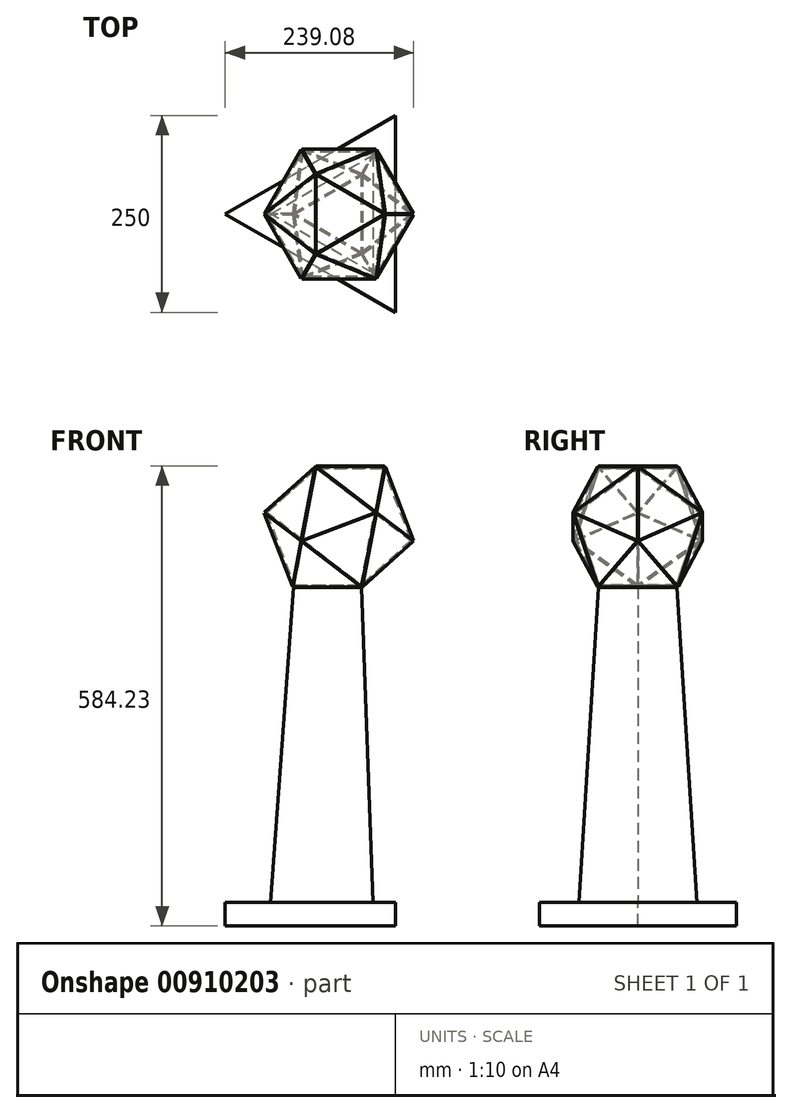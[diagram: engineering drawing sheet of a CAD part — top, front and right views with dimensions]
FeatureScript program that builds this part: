
annotation { "Feature Type Name" : "Feature", "Feature Type Description" : "" }
export const myFeature = defineFeature(function(context is Context, id is Id, definition is map)
    precondition{}
    {
        {
            var Q0;
            Q0=qCreatedBy(makeId("Top.planeOp"),FACE);
            var sketch = newSketch(context, id + "F0", { "sketchPlane" : qUnion([Q0])});
            skCircle(sketch, "E0.cCircle", {"center": v(0, 0) * mm, "radius": 28.87 * mm, "construction": true});
            skLineSegment(sketch, "E0.0", {"start": v(28.87, 50) * mm, "end": v(28.87, -50) * mm});
            skLineSegment(sketch, "E0.1", {"start": v(28.87, -50) * mm, "end": v(-57.74, 0) * mm});
            skLineSegment(sketch, "E0.2", {"start": v(-57.74, 0) * mm, "end": v(28.87, 50) * mm});
            skPoint(sketch, "E0.0.midPoint", {"position": v(28.87, 0) * mm});
            skSolve(sketch);
        }
        {
            var Q0;
            Q0=makeQuery(id+"F0.imprint","IMPRINT",FACE,{"disambiguationData":[TD([[makeQuery(id+"F0.imprint","IMPRINT",EDGE,{"derivedFrom":sQuery(id+"F0.wireOp",EDGE,"E0.0")}),-1.0]])]});
            extrude(context, id + "F1", {"entities" : qUnion([Q0]), "depth" : 3 * mm, "offsetDistance" : 25 * mm});
        }
        {
            var Q0;
            Q0=makeQuery(id+"F1.opExtrude","SWEPT_BODY",BODY,{"disambiguationData":[OSD([sQuery(id+"F0.wireOp",EDGE,"E0.0"),sQuery(id+"F0.wireOp",EDGE,"E0.1"),sQuery(id+"F0.wireOp",EDGE,"E0.2")])]});
            transform(context, id + "F2", {"entities" : qUnion([Q0]), "transformType" : TransformType.TRANSLATION_3D, "dx" : 0 * mm, "dy" : 0 * mm, "dz" : 0 * mm, "makeCopy" : true});
        }
        {
            var Q0;
            Q0=makeQuery(id+"F1.opExtrude","SWEPT_FACE",FACE,{"disambiguationData":[OSD([sQuery(id+"F0.wireOp",EDGE,"E0.1")])]});
            var sketch = newSketch(context, id + "F3", { "sketchPlane" : qUnion([Q0])});
            skLineSegment(sketch, "E1", {"start": v(-50, 1.5) * mm, "end": v(50, 1.5) * mm});
            skSolve(sketch);
        }
        {
            var Q0;
            Q0=makeQuery(id+"F2.opPattern","COPY",BODY,{"derivedFrom":makeQuery(id+"F1.opExtrude","SWEPT_BODY",BODY,{"disambiguationData":[OSD([sQuery(id+"F0.wireOp",EDGE,"E0.0"),sQuery(id+"F0.wireOp",EDGE,"E0.1"),sQuery(id+"F0.wireOp",EDGE,"E0.2")])]}),"instanceName":"1"});
            var Q1;
            Q1=sQuery(id+"F3.wireOp",EDGE,"E1");
            transform(context, id + "F4", {"entities" : qUnion([Q0]), "transformType" : TransformType.ROTATION, "transformAxis" : qUnion([Q1]), "angle" : 138.2 * degree, "makeCopy" : false});
        }
        {
            var Q0;
            Q0=makeQuery(id+"F1.opExtrude","SWEPT_BODY",BODY,{"disambiguationData":[OSD([sQuery(id+"F0.wireOp",EDGE,"E0.0"),sQuery(id+"F0.wireOp",EDGE,"E0.1"),sQuery(id+"F0.wireOp",EDGE,"E0.2")])]});
            transform(context, id + "F5", {"entities" : qUnion([Q0]), "transformType" : TransformType.TRANSLATION_3D, "dx" : 0 * mm, "dy" : 0 * mm, "dz" : 0 * mm, "makeCopy" : true});
        }
        {
            var Q0;
            Q0=makeQuery(id+"F1.opExtrude","SWEPT_FACE",FACE,{"disambiguationData":[OSD([sQuery(id+"F0.wireOp",EDGE,"E0.0")])]});
            var sketch = newSketch(context, id + "F6", { "sketchPlane" : qUnion([Q0])});
            skLineSegment(sketch, "E2", {"start": v(-50, 1.5) * mm, "end": v(50, 1.5) * mm});
            skSolve(sketch);
        }
        {
            var Q0;
            Q0=makeQuery(id+"F5.opPattern","COPY",BODY,{"derivedFrom":makeQuery(id+"F1.opExtrude","SWEPT_BODY",BODY,{"disambiguationData":[OSD([sQuery(id+"F0.wireOp",EDGE,"E0.0"),sQuery(id+"F0.wireOp",EDGE,"E0.1"),sQuery(id+"F0.wireOp",EDGE,"E0.2")])]}),"instanceName":"1"});
            var Q1;
            Q1=sQuery(id+"F6.wireOp",EDGE,"E2");
            transform(context, id + "F7", {"entities" : qUnion([Q0]), "transformType" : TransformType.ROTATION, "transformAxis" : qUnion([Q1]), "angle" : 138.2 * degree, "makeCopy" : false});
        }
        {
            var Q0;
            Q0=makeQuery(id+"F1.opExtrude","SWEPT_BODY",BODY,{"disambiguationData":[OSD([sQuery(id+"F0.wireOp",EDGE,"E0.0"),sQuery(id+"F0.wireOp",EDGE,"E0.1"),sQuery(id+"F0.wireOp",EDGE,"E0.2")])]});
            transform(context, id + "F8", {"entities" : qUnion([Q0]), "transformType" : TransformType.TRANSLATION_3D, "dx" : 0 * mm, "dy" : 0 * mm, "dz" : 0 * mm, "makeCopy" : true});
        }
        {
            var Q0;
            Q0=makeQuery(id+"F1.opExtrude","SWEPT_FACE",FACE,{"disambiguationData":[OSD([sQuery(id+"F0.wireOp",EDGE,"E0.2")])]});
            var sketch = newSketch(context, id + "F9", { "sketchPlane" : qUnion([Q0])});
            skLineSegment(sketch, "E3", {"start": v(-50, 1.5) * mm, "end": v(50, 1.5) * mm});
            skSolve(sketch);
        }
        {
            var Q0;
            Q0=makeQuery(id+"F8.opPattern","COPY",BODY,{"derivedFrom":makeQuery(id+"F1.opExtrude","SWEPT_BODY",BODY,{"disambiguationData":[OSD([sQuery(id+"F0.wireOp",EDGE,"E0.0"),sQuery(id+"F0.wireOp",EDGE,"E0.1"),sQuery(id+"F0.wireOp",EDGE,"E0.2")])]}),"instanceName":"1"});
            var Q1;
            Q1=sQuery(id+"F9.wireOp",EDGE,"E3");
            transform(context, id + "F10", {"entities" : qUnion([Q0]), "transformType" : TransformType.ROTATION, "transformAxis" : qUnion([Q1]), "angle" : 138.2 * degree, "makeCopy" : false});
        }
        {
            var Q0;
            Q0=makeQuery(id+"F2.opPattern","COPY",FACE,{"derivedFrom":makeQuery(id+"F1.opExtrude","SWEPT_FACE",FACE,{"disambiguationData":[OSD([sQuery(id+"F0.wireOp",EDGE,"E0.2")])]}),"instanceName":"1"});
            var sketch = newSketch(context, id + "F11", { "sketchPlane" : qUnion([Q0])});
            skLineSegment(sketch, "E4", {"start": v(87.46, 40.13) * mm, "end": v(6.05, -17.95) * mm});
            skSolve(sketch);
        }
        {
            var Q0;
            Q0=makeQuery(id+"F8.opPattern","COPY",FACE,{"derivedFrom":makeQuery(id+"F1.opExtrude","SWEPT_FACE",FACE,{"disambiguationData":[OSD([sQuery(id+"F0.wireOp",EDGE,"E0.1")])]}),"instanceName":"1"});
            var sketch = newSketch(context, id + "F12", { "sketchPlane" : qUnion([Q0])});
            skLineSegment(sketch, "E5", {"start": v(-87.46, 40.13) * mm, "end": v(-6.05, -17.95) * mm});
            skSolve(sketch);
        }
        {
            var Q0;
            Q0=makeQuery(id+"F2.opPattern","COPY",BODY,{"derivedFrom":makeQuery(id+"F1.opExtrude","SWEPT_BODY",BODY,{"disambiguationData":[OSD([sQuery(id+"F0.wireOp",EDGE,"E0.0"),sQuery(id+"F0.wireOp",EDGE,"E0.1"),sQuery(id+"F0.wireOp",EDGE,"E0.2")])]}),"instanceName":"1"});
            transform(context, id + "F13", {"entities" : qUnion([Q0]), "transformType" : TransformType.TRANSLATION_3D, "dx" : 0 * mm, "dy" : 0 * mm, "dz" : 0 * mm, "makeCopy" : true});
        }
        {
            var Q0;
            Q0=makeQuery(id+"F13.opPattern","COPY",BODY,{"derivedFrom":makeQuery(id+"F2.opPattern","COPY",BODY,{"derivedFrom":makeQuery(id+"F1.opExtrude","SWEPT_BODY",BODY,{"disambiguationData":[OSD([sQuery(id+"F0.wireOp",EDGE,"E0.0"),sQuery(id+"F0.wireOp",EDGE,"E0.1"),sQuery(id+"F0.wireOp",EDGE,"E0.2")])]}),"instanceName":"1"}),"instanceName":"1"});
            var Q1;
            Q1=sQuery(id+"F11.wireOp",EDGE,"E4");
            transform(context, id + "F14", {"entities" : qUnion([Q0]), "transformType" : TransformType.ROTATION, "transformAxis" : qUnion([Q1]), "angle" : 138.2 * degree, "oppositeDirection" : true, "makeCopy" : false});
        }
        {
            var Q0;
            Q0=makeQuery(id+"F8.opPattern","COPY",BODY,{"derivedFrom":makeQuery(id+"F1.opExtrude","SWEPT_BODY",BODY,{"disambiguationData":[OSD([sQuery(id+"F0.wireOp",EDGE,"E0.0"),sQuery(id+"F0.wireOp",EDGE,"E0.1"),sQuery(id+"F0.wireOp",EDGE,"E0.2")])]}),"instanceName":"1"});
            transform(context, id + "F15", {"entities" : qUnion([Q0]), "transformType" : TransformType.TRANSLATION_3D, "dx" : 0 * mm, "dy" : 0 * mm, "dz" : 0 * mm, "makeCopy" : true});
        }
        {
            var Q0;
            Q0=makeQuery(id+"F15.opPattern","COPY",BODY,{"derivedFrom":makeQuery(id+"F8.opPattern","COPY",BODY,{"derivedFrom":makeQuery(id+"F1.opExtrude","SWEPT_BODY",BODY,{"disambiguationData":[OSD([sQuery(id+"F0.wireOp",EDGE,"E0.0"),sQuery(id+"F0.wireOp",EDGE,"E0.1"),sQuery(id+"F0.wireOp",EDGE,"E0.2")])]}),"instanceName":"1"}),"instanceName":"1"});
            var Q1;
            Q1=sQuery(id+"F12.wireOp",EDGE,"E5");
            transform(context, id + "F16", {"entities" : qUnion([Q0]), "transformType" : TransformType.ROTATION, "transformAxis" : qUnion([Q1]), "angle" : 138.2 * degree, "makeCopy" : false});
        }
        {
            var Q0;
            Q0=makeQuery(id+"F8.opPattern","COPY",FACE,{"derivedFrom":makeQuery(id+"F1.opExtrude","SWEPT_FACE",FACE,{"disambiguationData":[OSD([sQuery(id+"F0.wireOp",EDGE,"E0.0")])]}),"instanceName":"1"});
            var sketch = newSketch(context, id + "F17", { "sketchPlane" : qUnion([Q0])});
            skLineSegment(sketch, "E6", {"start": v(2.28, -18.8) * mm, "end": v(93.78, 21.55) * mm});
            skSolve(sketch);
        }
        {
            var Q0;
            Q0=makeQuery(id+"F8.opPattern","COPY",BODY,{"derivedFrom":makeQuery(id+"F1.opExtrude","SWEPT_BODY",BODY,{"disambiguationData":[OSD([sQuery(id+"F0.wireOp",EDGE,"E0.0"),sQuery(id+"F0.wireOp",EDGE,"E0.1"),sQuery(id+"F0.wireOp",EDGE,"E0.2")])]}),"instanceName":"1"});
            transform(context, id + "F18", {"entities" : qUnion([Q0]), "transformType" : TransformType.TRANSLATION_3D, "dx" : 0 * mm, "dy" : 0 * mm, "dz" : 0 * mm, "makeCopy" : true});
        }
        {
            var Q0;
            Q0=makeQuery(id+"F8.opPattern","COPY",BODY,{"derivedFrom":makeQuery(id+"F1.opExtrude","SWEPT_BODY",BODY,{"disambiguationData":[OSD([sQuery(id+"F0.wireOp",EDGE,"E0.0"),sQuery(id+"F0.wireOp",EDGE,"E0.1"),sQuery(id+"F0.wireOp",EDGE,"E0.2")])]}),"instanceName":"1"});
            var Q1;
            Q1=sQuery(id+"F17.wireOp",EDGE,"E6");
            transform(context, id + "F19", {"entities" : qUnion([Q0]), "transformType" : TransformType.ROTATION, "transformAxis" : qUnion([Q1]), "angle" : 138.2 * degree, "makeCopy" : false});
        }
        {
            var Q0;
            Q0=qCreatedBy(makeId("Right.planeOp"),FACE);
            var sketch = newSketch(context, id + "F20", { "sketchPlane" : qUnion([Q0])});
            skLineSegment(sketch, "E7", {"start": v(0, 0) * mm, "end": v(0, 167.31) * mm});
            skSolve(sketch);
        }
        {
            var Q0;
            Q0=makeQuery(id+"F18.opPattern","COPY",BODY,{"derivedFrom":makeQuery(id+"F8.opPattern","COPY",BODY,{"derivedFrom":makeQuery(id+"F1.opExtrude","SWEPT_BODY",BODY,{"disambiguationData":[OSD([sQuery(id+"F0.wireOp",EDGE,"E0.0"),sQuery(id+"F0.wireOp",EDGE,"E0.1"),sQuery(id+"F0.wireOp",EDGE,"E0.2")])]}),"instanceName":"1"}),"instanceName":"1"});
            var Q1;
            Q1=sQuery(id+"F20.wireOp",EDGE,"E7");
            circularPattern(context, id + "F21", {"entities" : qUnion([Q0]), "axis" : qUnion([Q1]), "angle" : 360 * degree, "instanceCount" : 3, "equalSpace" : true});
        }
        {
            var Q0;
            Q0=makeQuery(id+"F15.opPattern","COPY",BODY,{"derivedFrom":makeQuery(id+"F8.opPattern","COPY",BODY,{"derivedFrom":makeQuery(id+"F1.opExtrude","SWEPT_BODY",BODY,{"disambiguationData":[OSD([sQuery(id+"F0.wireOp",EDGE,"E0.0"),sQuery(id+"F0.wireOp",EDGE,"E0.1"),sQuery(id+"F0.wireOp",EDGE,"E0.2")])]}),"instanceName":"1"}),"instanceName":"1"});
            var Q1;
            Q1=sQuery(id+"F20.wireOp",EDGE,"E7");
            circularPattern(context, id + "F22", {"entities" : qUnion([Q0]), "axis" : qUnion([Q1]), "angle" : 360 * degree, "instanceCount" : 3, "equalSpace" : true});
        }
        {
            var Q0;
            Q0=makeQuery(id+"F8.opPattern","COPY",BODY,{"derivedFrom":makeQuery(id+"F1.opExtrude","SWEPT_BODY",BODY,{"disambiguationData":[OSD([sQuery(id+"F0.wireOp",EDGE,"E0.0"),sQuery(id+"F0.wireOp",EDGE,"E0.1"),sQuery(id+"F0.wireOp",EDGE,"E0.2")])]}),"instanceName":"1"});
            var Q1;
            Q1=sQuery(id+"F20.wireOp",EDGE,"E7");
            circularPattern(context, id + "F23", {"entities" : qUnion([Q0]), "axis" : qUnion([Q1]), "angle" : 360 * degree, "instanceCount" : 3, "equalSpace" : true});
        }
        {
            var Q0;
            Q0=makeQuery(id+"F15.opPattern","COPY",FACE,{"derivedFrom":makeQuery(id+"F8.opPattern","COPY",FACE,{"derivedFrom":makeQuery(id+"F1.opExtrude","SWEPT_FACE",FACE,{"disambiguationData":[OSD([sQuery(id+"F0.wireOp",EDGE,"E0.0")])]}),"instanceName":"1"}),"instanceName":"1"});
            var sketch = newSketch(context, id + "F24", { "sketchPlane" : qUnion([Q0])});
            skLineSegment(sketch, "E8", {"start": v(-80.56, -44.79) * mm, "end": v(-33.35, 43.37) * mm});
            skSolve(sketch);
        }
        {
            var Q0;
            Q0=makeQuery(id+"F15.opPattern","COPY",BODY,{"derivedFrom":makeQuery(id+"F8.opPattern","COPY",BODY,{"derivedFrom":makeQuery(id+"F1.opExtrude","SWEPT_BODY",BODY,{"disambiguationData":[OSD([sQuery(id+"F0.wireOp",EDGE,"E0.0"),sQuery(id+"F0.wireOp",EDGE,"E0.1"),sQuery(id+"F0.wireOp",EDGE,"E0.2")])]}),"instanceName":"1"}),"instanceName":"1"});
            transform(context, id + "F25", {"entities" : qUnion([Q0]), "transformType" : TransformType.TRANSLATION_3D, "dx" : 0 * mm, "dy" : 0 * mm, "dz" : 0 * mm, "makeCopy" : true});
        }
        {
            var Q0;
            Q0=makeQuery(id+"F25.opPattern","COPY",BODY,{"derivedFrom":makeQuery(id+"F15.opPattern","COPY",BODY,{"derivedFrom":makeQuery(id+"F8.opPattern","COPY",BODY,{"derivedFrom":makeQuery(id+"F1.opExtrude","SWEPT_BODY",BODY,{"disambiguationData":[OSD([sQuery(id+"F0.wireOp",EDGE,"E0.0"),sQuery(id+"F0.wireOp",EDGE,"E0.1"),sQuery(id+"F0.wireOp",EDGE,"E0.2")])]}),"instanceName":"1"}),"instanceName":"1"}),"instanceName":"1"});
            var Q1;
            Q1=sQuery(id+"F24.wireOp",EDGE,"E8");
            transform(context, id + "F26", {"entities" : qUnion([Q0]), "transformType" : TransformType.ROTATION, "transformAxis" : qUnion([Q1]), "angle" : 138.2 * degree, "oppositeDirection" : true, "makeCopy" : false});
        }
        {
            var Q0;
            Q0=makeQuery(id+"F25.opPattern","COPY",BODY,{"derivedFrom":makeQuery(id+"F15.opPattern","COPY",BODY,{"derivedFrom":makeQuery(id+"F8.opPattern","COPY",BODY,{"derivedFrom":makeQuery(id+"F1.opExtrude","SWEPT_BODY",BODY,{"disambiguationData":[OSD([sQuery(id+"F0.wireOp",EDGE,"E0.0"),sQuery(id+"F0.wireOp",EDGE,"E0.1"),sQuery(id+"F0.wireOp",EDGE,"E0.2")])]}),"instanceName":"1"}),"instanceName":"1"}),"instanceName":"1"});
            var Q1;
            Q1=sQuery(id+"F20.wireOp",EDGE,"E7");
            circularPattern(context, id + "F27", {"entities" : qUnion([Q0]), "axis" : qUnion([Q1]), "angle" : 360 * degree, "instanceCount" : 3, "equalSpace" : true});
        }
        {
            var Q0;
            Q0=makeQuery(id+"F13.opPattern","COPY",BODY,{"derivedFrom":makeQuery(id+"F2.opPattern","COPY",BODY,{"derivedFrom":makeQuery(id+"F1.opExtrude","SWEPT_BODY",BODY,{"disambiguationData":[OSD([sQuery(id+"F0.wireOp",EDGE,"E0.0"),sQuery(id+"F0.wireOp",EDGE,"E0.1"),sQuery(id+"F0.wireOp",EDGE,"E0.2")])]}),"instanceName":"1"}),"instanceName":"1"});
            transform(context, id + "F28", {"entities" : qUnion([Q0]), "transformType" : TransformType.TRANSLATION_3D, "dx" : 0 * mm, "dy" : 0 * mm, "dz" : 0 * mm, "makeCopy" : true});
        }
        {
            var Q0;
            Q0=makeQuery(id+"F13.opPattern","COPY",FACE,{"derivedFrom":makeQuery(id+"F2.opPattern","COPY",FACE,{"derivedFrom":makeQuery(id+"F1.opExtrude","SWEPT_FACE",FACE,{"disambiguationData":[OSD([sQuery(id+"F0.wireOp",EDGE,"E0.0")])]}),"instanceName":"1"}),"instanceName":"1"});
            var sketch = newSketch(context, id + "F29", { "sketchPlane" : qUnion([Q0])});
            skLineSegment(sketch, "E9", {"start": v(-80.56, 44.79) * mm, "end": v(-33.35, -43.37) * mm});
            skSolve(sketch);
        }
        {
            var Q0;
            Q0=makeQuery(id+"F28.opPattern","COPY",BODY,{"derivedFrom":makeQuery(id+"F13.opPattern","COPY",BODY,{"derivedFrom":makeQuery(id+"F2.opPattern","COPY",BODY,{"derivedFrom":makeQuery(id+"F1.opExtrude","SWEPT_BODY",BODY,{"disambiguationData":[OSD([sQuery(id+"F0.wireOp",EDGE,"E0.0"),sQuery(id+"F0.wireOp",EDGE,"E0.1"),sQuery(id+"F0.wireOp",EDGE,"E0.2")])]}),"instanceName":"1"}),"instanceName":"1"}),"instanceName":"1"});
            var Q1;
            Q1=sQuery(id+"F29.wireOp",EDGE,"E9");
            transform(context, id + "F30", {"entities" : qUnion([Q0]), "transformType" : TransformType.ROTATION, "transformAxis" : qUnion([Q1]), "angle" : 138.2 * degree, "makeCopy" : false});
        }
        {
            var Q0;
            Q0=makeQuery(id+"F28.opPattern","COPY",BODY,{"derivedFrom":makeQuery(id+"F13.opPattern","COPY",BODY,{"derivedFrom":makeQuery(id+"F2.opPattern","COPY",BODY,{"derivedFrom":makeQuery(id+"F1.opExtrude","SWEPT_BODY",BODY,{"disambiguationData":[OSD([sQuery(id+"F0.wireOp",EDGE,"E0.0"),sQuery(id+"F0.wireOp",EDGE,"E0.1"),sQuery(id+"F0.wireOp",EDGE,"E0.2")])]}),"instanceName":"1"}),"instanceName":"1"}),"instanceName":"1"});
            var Q1;
            Q1=sQuery(id+"F20.wireOp",EDGE,"E7");
            circularPattern(context, id + "F31", {"entities" : qUnion([Q0]), "axis" : qUnion([Q1]), "angle" : 360 * degree, "instanceCount" : 3, "equalSpace" : true});
        }
        {
            var Q0;
            Q0=makeQuery(id+"F28.opPattern","COPY",BODY,{"derivedFrom":makeQuery(id+"F13.opPattern","COPY",BODY,{"derivedFrom":makeQuery(id+"F2.opPattern","COPY",BODY,{"derivedFrom":makeQuery(id+"F1.opExtrude","SWEPT_BODY",BODY,{"disambiguationData":[OSD([sQuery(id+"F0.wireOp",EDGE,"E0.0"),sQuery(id+"F0.wireOp",EDGE,"E0.1"),sQuery(id+"F0.wireOp",EDGE,"E0.2")])]}),"instanceName":"1"}),"instanceName":"1"}),"instanceName":"1"});
            transform(context, id + "F32", {"entities" : qUnion([Q0]), "transformType" : TransformType.TRANSLATION_3D, "dx" : 0 * mm, "dy" : 0 * mm, "dz" : 0 * mm, "makeCopy" : true});
        }
        {
            var Q0;
            Q0=makeQuery(id+"F28.opPattern","COPY",FACE,{"derivedFrom":makeQuery(id+"F13.opPattern","COPY",FACE,{"derivedFrom":makeQuery(id+"F2.opPattern","COPY",FACE,{"derivedFrom":makeQuery(id+"F1.opExtrude","SWEPT_FACE",FACE,{"disambiguationData":[OSD([sQuery(id+"F0.wireOp",EDGE,"E0.1")])]}),"instanceName":"1"}),"instanceName":"1"}),"instanceName":"1"});
            var sketch = newSketch(context, id + "F33", { "sketchPlane" : qUnion([Q0])});
            skLineSegment(sketch, "E10", {"start": v(-14.7, -137.74) * mm, "end": v(-80.15, -62.13) * mm});
            skSolve(sketch);
        }
        {
            var Q0;
            Q0=makeQuery(id+"F28.opPattern","COPY",BODY,{"derivedFrom":makeQuery(id+"F13.opPattern","COPY",BODY,{"derivedFrom":makeQuery(id+"F2.opPattern","COPY",BODY,{"derivedFrom":makeQuery(id+"F1.opExtrude","SWEPT_BODY",BODY,{"disambiguationData":[OSD([sQuery(id+"F0.wireOp",EDGE,"E0.0"),sQuery(id+"F0.wireOp",EDGE,"E0.1"),sQuery(id+"F0.wireOp",EDGE,"E0.2")])]}),"instanceName":"1"}),"instanceName":"1"}),"instanceName":"1"});
            var Q1;
            Q1=sQuery(id+"F33.wireOp",EDGE,"E10");
            var Q2;
            Q2=sQuery(id+"F33.wireOp",EDGE,"E10");
            transform(context, id + "F34", {"entities" : qUnion([Q0]), "transformType" : TransformType.ROTATION, "transformAxis" : qUnion([Q2]), "angle" : 138.2 * degree, "oppositeDirection" : true, "makeCopy" : false});
        }
        {
            var Q0;
            Q0=makeQuery(id+"F28.opPattern","COPY",BODY,{"derivedFrom":makeQuery(id+"F13.opPattern","COPY",BODY,{"derivedFrom":makeQuery(id+"F2.opPattern","COPY",BODY,{"derivedFrom":makeQuery(id+"F1.opExtrude","SWEPT_BODY",BODY,{"disambiguationData":[OSD([sQuery(id+"F0.wireOp",EDGE,"E0.0"),sQuery(id+"F0.wireOp",EDGE,"E0.1"),sQuery(id+"F0.wireOp",EDGE,"E0.2")])]}),"instanceName":"1"}),"instanceName":"1"}),"instanceName":"1"});
            var Q1;
            Q1=sQuery(id+"F20.wireOp",EDGE,"E7");
            circularPattern(context, id + "F35", {"entities" : qUnion([Q0]), "axis" : qUnion([Q1]), "angle" : 360 * degree, "instanceCount" : 3, "equalSpace" : true});
        }
        {
            var Q0;
            Q0=makeQuery(id+"F28.opPattern","COPY",BODY,{"derivedFrom":makeQuery(id+"F13.opPattern","COPY",BODY,{"derivedFrom":makeQuery(id+"F2.opPattern","COPY",BODY,{"derivedFrom":makeQuery(id+"F1.opExtrude","SWEPT_BODY",BODY,{"disambiguationData":[OSD([sQuery(id+"F0.wireOp",EDGE,"E0.0"),sQuery(id+"F0.wireOp",EDGE,"E0.1"),sQuery(id+"F0.wireOp",EDGE,"E0.2")])]}),"instanceName":"1"}),"instanceName":"1"}),"instanceName":"1"});
            transform(context, id + "F36", {"entities" : qUnion([Q0]), "transformType" : TransformType.TRANSLATION_3D, "dx" : 0 * mm, "dy" : 0 * mm, "dz" : 0 * mm, "makeCopy" : true});
        }
        {
            var Q0;
            Q0=makeQuery(id+"F28.opPattern","COPY",BODY,{"derivedFrom":makeQuery(id+"F13.opPattern","COPY",BODY,{"derivedFrom":makeQuery(id+"F2.opPattern","COPY",BODY,{"derivedFrom":makeQuery(id+"F1.opExtrude","SWEPT_BODY",BODY,{"disambiguationData":[OSD([sQuery(id+"F0.wireOp",EDGE,"E0.0"),sQuery(id+"F0.wireOp",EDGE,"E0.1"),sQuery(id+"F0.wireOp",EDGE,"E0.2")])]}),"instanceName":"1"}),"instanceName":"1"}),"instanceName":"1"});
            transform(context, id + "F37", {"entities" : qUnion([Q0]), "transformType" : TransformType.TRANSLATION_3D, "dx" : 0 * mm, "dy" : 0 * mm, "dz" : 0 * mm, "makeCopy" : true});
        }
        {
            var Q0;
            Q0=makeQuery(id+"F28.opPattern","COPY",FACE,{"derivedFrom":makeQuery(id+"F13.opPattern","COPY",FACE,{"derivedFrom":makeQuery(id+"F2.opPattern","COPY",FACE,{"derivedFrom":makeQuery(id+"F1.opExtrude","SWEPT_FACE",FACE,{"disambiguationData":[OSD([sQuery(id+"F0.wireOp",EDGE,"E0.2")])]}),"instanceName":"1"}),"instanceName":"1"}),"instanceName":"1"});
            var sketch = newSketch(context, id + "F38", { "sketchPlane" : qUnion([Q0])});
            skLineSegment(sketch, "E11", {"start": v(-50.02, 133.02) * mm, "end": v(49.98, 133.06) * mm});
            skSolve(sketch);
        }
        {
            var Q0;
            Q0=makeQuery(id+"F28.opPattern","COPY",BODY,{"derivedFrom":makeQuery(id+"F13.opPattern","COPY",BODY,{"derivedFrom":makeQuery(id+"F2.opPattern","COPY",BODY,{"derivedFrom":makeQuery(id+"F1.opExtrude","SWEPT_BODY",BODY,{"disambiguationData":[OSD([sQuery(id+"F0.wireOp",EDGE,"E0.0"),sQuery(id+"F0.wireOp",EDGE,"E0.1"),sQuery(id+"F0.wireOp",EDGE,"E0.2")])]}),"instanceName":"1"}),"instanceName":"1"}),"instanceName":"1"});
            var Q1;
            Q1=makeQuery(id+"F37.opPattern","COPY",BODY,{"derivedFrom":makeQuery(id+"F28.opPattern","COPY",BODY,{"derivedFrom":makeQuery(id+"F13.opPattern","COPY",BODY,{"derivedFrom":makeQuery(id+"F2.opPattern","COPY",BODY,{"derivedFrom":makeQuery(id+"F1.opExtrude","SWEPT_BODY",BODY,{"disambiguationData":[OSD([sQuery(id+"F0.wireOp",EDGE,"E0.0"),sQuery(id+"F0.wireOp",EDGE,"E0.1"),sQuery(id+"F0.wireOp",EDGE,"E0.2")])]}),"instanceName":"1"}),"instanceName":"1"}),"instanceName":"1"}),"instanceName":"1"});
            var Q2;
            Q2=sQuery(id+"F38.wireOp",EDGE,"E11");
            transform(context, id + "F39", {"entities" : qUnion([Q0, Q1]), "transformType" : TransformType.ROTATION, "transformAxis" : qUnion([Q2]), "angle" : 138.2 * degree, "oppositeDirection" : true, "makeCopy" : false});
        }
        {
            var Q0;
            Q0=makeQuery(id+"F1.opExtrude","CAP_FACE",FACE,{"disambiguationData":[OSD([sQuery(id+"F0.wireOp",EDGE,"E0.0"),sQuery(id+"F0.wireOp",EDGE,"E0.1"),sQuery(id+"F0.wireOp",EDGE,"E0.2")])],"isStart":true});
            var sketch = newSketch(context, id + "F40", { "sketchPlane" : qUnion([Q0])});
            skCircle(sketch, "E12.cCircle", {"center": v(0, 0) * mm, "radius": 28.87 * mm, "construction": true});
            skLineSegment(sketch, "E12.0", {"start": v(-57.74, 0) * mm, "end": v(28.87, 50) * mm});
            skLineSegment(sketch, "E12.1", {"start": v(28.87, 50) * mm, "end": v(28.87, -50) * mm});
            skLineSegment(sketch, "E12.2", {"start": v(28.87, -50) * mm, "end": v(-57.74, 0) * mm});
            skPoint(sketch, "E12.0.midPoint", {"position": v(-14.43, 25) * mm});
            skSolve(sketch);
        }
        {
            var Q0;
            Q0=qCreatedBy(makeId("Top.planeOp"),FACE);
            cPlane(context, id + "F41", {"entities" : qUnion([Q0]), "cplaneType" : CPlaneType.OFFSET, "offset" : 400 * mm, "oppositeDirection" : true, "width" : 150 * mm, "height" : 150 * mm});
        }
        {
            var Q0;
            Q0=qCreatedBy(id+"F41.planeOp",FACE);
            var sketch = newSketch(context, id + "F42", { "sketchPlane" : qUnion([Q0])});
            skCircle(sketch, "E13.cCircle", {"center": v(0, 0) * mm, "radius": 43.3 * mm, "construction": true});
            skLineSegment(sketch, "E13.0", {"start": v(43.3, 75) * mm, "end": v(43.3, -75) * mm});
            skLineSegment(sketch, "E13.1", {"start": v(43.3, -75) * mm, "end": v(-86.6, 0) * mm});
            skLineSegment(sketch, "E13.2", {"start": v(-86.6, 0) * mm, "end": v(43.3, 75) * mm});
            skPoint(sketch, "E13.0.midPoint", {"position": v(43.3, 0) * mm});
            skSolve(sketch);
        }
        {
            var Q1;
            Q1=makeQuery(id+"F40.imprint","IMPRINT",FACE,{"disambiguationData":[TD([[makeQuery(id+"F40.imprint","IMPRINT",EDGE,{"derivedFrom":sQuery(id+"F40.wireOp",EDGE,"E12.0")}),1.0]])]});
            var Q2;
            Q2=makeQuery(id+"F42.imprint","IMPRINT",FACE,{"disambiguationData":[TD([[makeQuery(id+"F42.imprint","IMPRINT",EDGE,{"derivedFrom":sQuery(id+"F42.wireOp",EDGE,"E13.0")}),-1.0]])]});
            loft(context, id + "F43", {"operationType" : NewBodyOperationType.ADD, "sheetProfilesArray" : [{ "sheetProfileEntities" : qUnion([Q1]) }, { "sheetProfileEntities" : qUnion([Q2]) }]});
        }
        {
            var Q0;
            Q0=makeQuery(id+"F43.opLoft","CAP_FACE",FACE,{"disambiguationData":[OSD([makeQuery(id+"F42.imprint","IMPRINT",FACE,{"disambiguationData":[TD([[makeQuery(id+"F42.imprint","IMPRINT",EDGE,{"derivedFrom":sQuery(id+"F42.wireOp",EDGE,"E13.0")}),-1.0]])]})])],"isStart":true});
            var sketch = newSketch(context, id + "F44", { "sketchPlane" : qUnion([Q0])});
            skCircle(sketch, "E14.cCircle", {"center": v(0, 0) * mm, "radius": 72.17 * mm, "construction": true});
            skLineSegment(sketch, "E14.0", {"start": v(72.17, 125) * mm, "end": v(72.17, -125) * mm});
            skLineSegment(sketch, "E14.1", {"start": v(72.17, -125) * mm, "end": v(-144.34, 0) * mm});
            skLineSegment(sketch, "E14.2", {"start": v(-144.34, 0) * mm, "end": v(72.17, 125) * mm});
            skPoint(sketch, "E14.0.midPoint", {"position": v(72.17, 0) * mm});
            skSolve(sketch);
        }
        {
            var Q0;
            Q0=makeQuery(id+"F44.imprint","IMPRINT",FACE,{"disambiguationData":[TD([[makeQuery(id+"F44.imprint","IMPRINT",EDGE,{"derivedFrom":sQuery(id+"F44.wireOp",EDGE,"E14.0")}),-1.0]])]});
            var Q1;
            {var subQ0=sQuery(id+"F42.wireOp",EDGE,"E13.0");var subQ1=sQuery(id+"F42.wireOp",EDGE,"E13.1");var subQ2=makeQuery(id+"F42.imprint","INTERSECT",VERTEX,{"derivedFrom":[subQ0,subQ1]});var subQ3=sQuery(id+"F42.wireOp",EDGE,"E13.2");var subQ4=makeQuery(id+"F42.imprint","INTERSECT",VERTEX,{"derivedFrom":[subQ0,subQ3]});Q1=makeQuery(id+"F44.imprint","IMPRINT",FACE,{"disambiguationData":[TD([[makeQuery(id+"F44.imprint","IMPRINT",EDGE,{"derivedFrom":makeQuery(id+"F43.opLoft","MID_CAP_EDGE",EDGE,{"disambiguationData":[OSD([subQ0,subQ1,subQ3]),TDD([subQ4,subQ2,makeQuery(id+"F42.imprint","IMPRINT",EDGE,{"derivedFrom":subQ0})])],"capPos":1.0})}),1.0]])]});}
            extrude(context, id + "F45", {"entities" : qUnion([Q0, Q1]), "operationType" : NewBodyOperationType.ADD, "depth" : 30 * mm, "offsetDistance" : 25 * mm});
        }
    });
